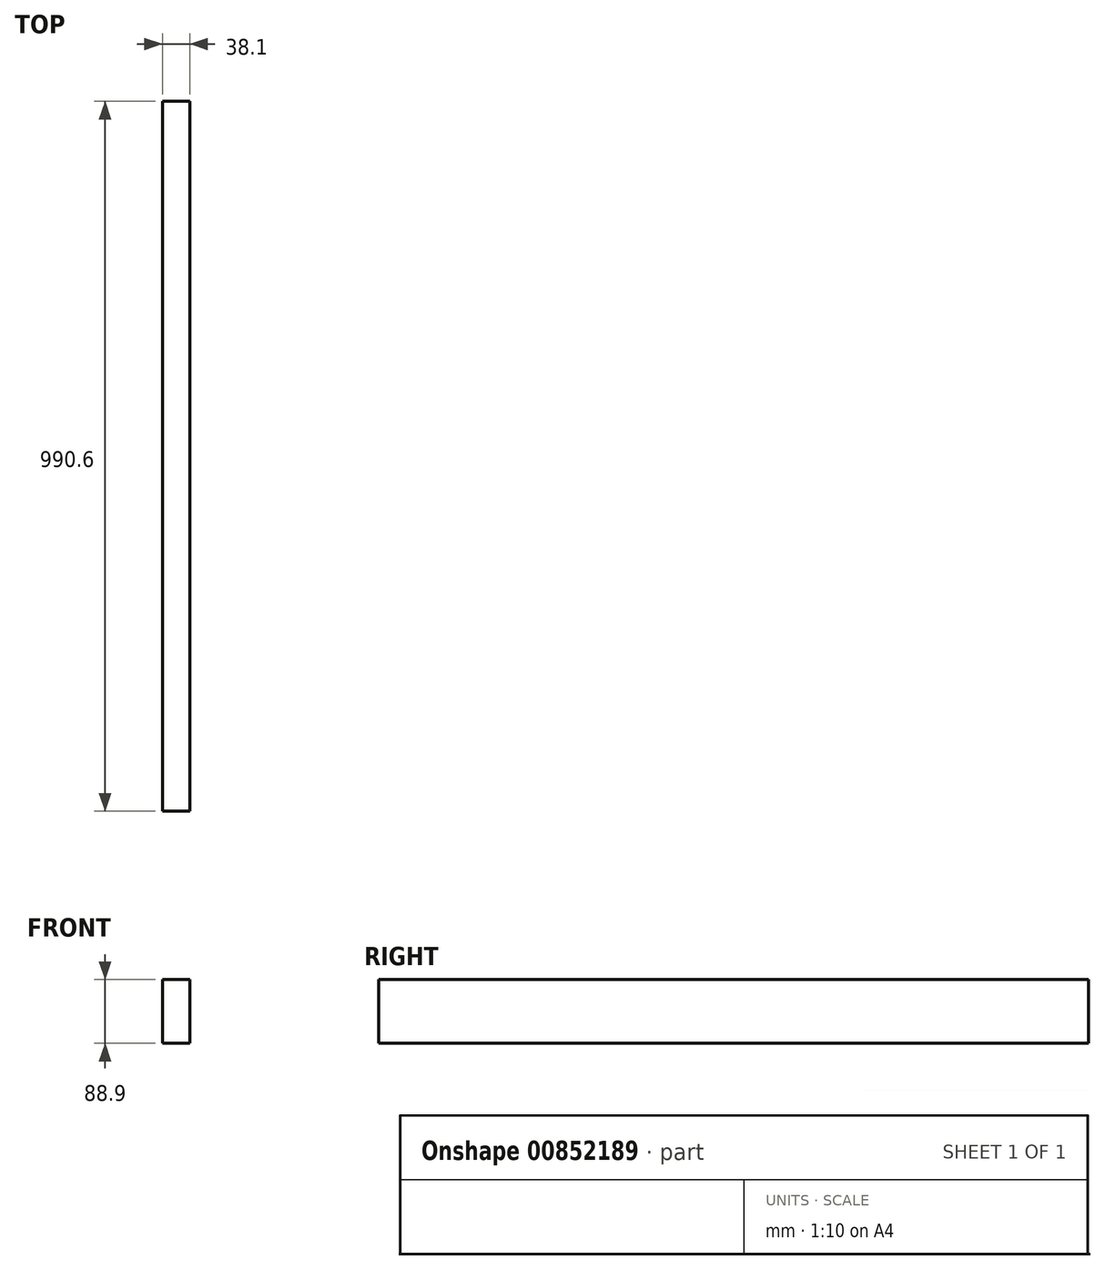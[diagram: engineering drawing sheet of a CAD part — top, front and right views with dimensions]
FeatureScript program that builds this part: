
annotation { "Feature Type Name" : "Feature", "Feature Type Description" : "" }
export const myFeature = defineFeature(function(context is Context, id is Id, definition is map)
    precondition{}
    {
        {
            var Q0;
            Q0=qCreatedBy(makeId("Front.planeOp"),FACE);
            var sketch = newSketch(context, id + "F0", { "sketchPlane" : qUnion([Q0])});
            skLineSegment(sketch, "E0.bottom", {"start": v(19.05, -44.45) * mm, "end": v(-19.05, -44.45) * mm});
            skLineSegment(sketch, "E0.top", {"start": v(19.05, 44.45) * mm, "end": v(-19.05, 44.45) * mm});
            skLineSegment(sketch, "E0.left", {"start": v(19.05, -44.45) * mm, "end": v(19.05, 44.45) * mm});
            skLineSegment(sketch, "E0.right", {"start": v(-19.05, -44.45) * mm, "end": v(-19.05, 44.45) * mm});
            skPoint(sketch, "E0.middle", {"position": v(0, 0) * mm});
            skSolve(sketch);
        }
        {
            var Q0;
            Q0=makeQuery(id+"F0.imprint","IMPRINT",FACE,{"disambiguationData":[TD([[makeQuery(id+"F0.imprint","IMPRINT",EDGE,{"derivedFrom":sQuery(id+"F0.wireOp",EDGE,"E0.bottom")}),-1.0]])]});
            extrude(context, id + "F1", {"entities" : qUnion([Q0]), "depth" : 990.6 * mm, "offsetDistance" : 25.4 * mm});
        }
    });
